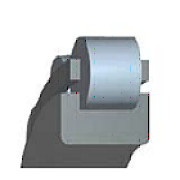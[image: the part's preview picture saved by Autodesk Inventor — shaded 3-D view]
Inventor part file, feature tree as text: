
AUTODESK INVENTOR PART (.ipt)
format: ipt  version: 2020 (Build 240168000, 168)  size: 168,960 bytes
history: native  units: mm (DEFAULTED — no unit token found)
features: sketch x1
ambient origin geometry x8: Origin, YZ Plane, XZ Plane, XY Plane, X Axis, Y Axis, Z Axis, Center Point
bodies: Solid1 (feature_tree), Body (feature_tree)
feature tree (1):
  sketch  "Sketch"  dims[d0=5.0mm d1=8.0mm d2=10.666667mm d3=16.0mm d4=90.0deg d5=0.3mm d6=0.0mm d7=0.0mm d8=0.0mm d9=0.0mm d10=0.0mm]
